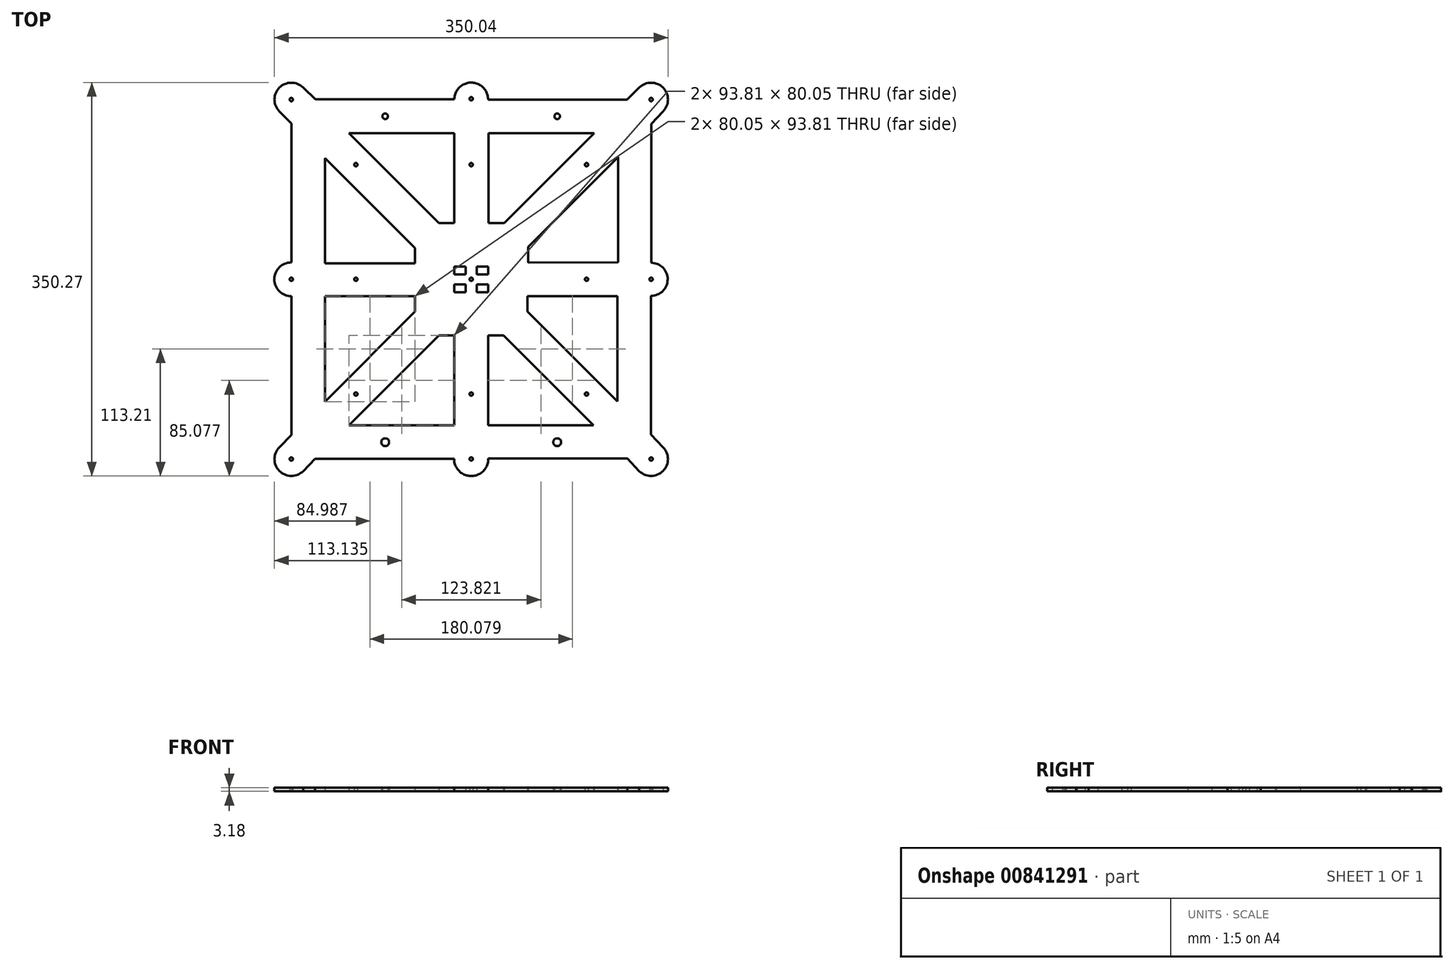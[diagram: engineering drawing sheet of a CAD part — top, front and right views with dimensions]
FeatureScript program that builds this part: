
annotation { "Feature Type Name" : "Feature", "Feature Type Description" : "" }
export const myFeature = defineFeature(function(context is Context, id is Id, definition is map)
    precondition{}
    {
        {
            var Q0;
            Q0=qCreatedBy(makeId("Top.planeOp"),FACE);
            var sketch = newSketch(context, id + "F0", { "sketchPlane" : qUnion([Q0])});
            skPoint(sketch, "E0.middle", {"position": v(0, 0) * mm});
            skLineSegment(sketch, "E1", {"start": v(-130.02, 107.83) * mm, "end": v(-130.02, 14.06) * mm});
            skLineSegment(sketch, "E2", {"start": v(-160.02, 138.65) * mm, "end": v(-160.02, 15.05) * mm});
            skLineSegment(sketch, "E3.MirrorCS", {"start": v(-138.62, 160.12) * mm, "end": v(-15.02, 160.12) * mm});
            skLineSegment(sketch, "E4.MirrorCS", {"start": v(-108.76, 130.12) * mm, "end": v(-14.99, 130.12) * mm});
            skLineSegment(sketch, "E5.MirrorCS", {"start": v(109.27, 130.02) * mm, "end": v(15.5, 130.02) * mm});
            skLineSegment(sketch, "E6.MirrorCS", {"start": v(160.27, 138.3) * mm, "end": v(160.27, 14.7) * mm});
            skLineSegment(sketch, "E7.MirrorCS", {"start": v(130.5, 108.82) * mm, "end": v(130.57, 15.05) * mm});
            skLineSegment(sketch, "E8.MirrorCS", {"start": v(-160, -138.65) * mm, "end": v(-160, -15.05) * mm});
            skLineSegment(sketch, "E9.MirrorCS", {"start": v(-130.04, -108.82) * mm, "end": v(-130.08, -15.05) * mm});
            skLineSegment(sketch, "E10.MirrorCS", {"start": v(-108.81, -130.03) * mm, "end": v(-15.04, -130.07) * mm});
            skLineSegment(sketch, "E11.MirrorCS", {"start": v(-138.84, -159.88) * mm, "end": v(-15.24, -159.88) * mm});
            skLineSegment(sketch, "E12.MirrorCS", {"start": v(108.82, -130.03) * mm, "end": v(15.05, -130.07) * mm});
            skLineSegment(sketch, "E13.MirrorCS", {"start": v(130.01, -108.8) * mm, "end": v(130.05, -15.03) * mm});
            skLineSegment(sketch, "E14.MirrorCS", {"start": v(160, -138.3) * mm, "end": v(160, -14.7) * mm});
            skLineSegment(sketch, "E15", {"start": v(-49.97, 14.06) * mm, "end": v(-130.02, 14.06) * mm});
            skLineSegment(sketch, "E16", {"start": v(-50.03, -15) * mm, "end": v(-130.08, -15.05) * mm});
            skLineSegment(sketch, "E17", {"start": v(-170.7, 149.5) * mm, "end": v(-160.02, 138.65) * mm});
            skLineSegment(sketch, "E18", {"start": v(-130.02, 107.83) * mm, "end": v(-49.97, 27.86) * mm});
            skLineSegment(sketch, "E19", {"start": v(-49.97, 27.86) * mm, "end": v(-49.97, 14.06) * mm});
            skLineSegment(sketch, "E20", {"start": v(-50.03, -15) * mm, "end": v(-50.03, -28.8) * mm});
            skLineSegment(sketch, "E21", {"start": v(-170.7, -149.5) * mm, "end": v(-160, -138.65) * mm});
            skLineSegment(sketch, "E22", {"start": v(-130.04, -108.82) * mm, "end": v(-50.03, -28.8) * mm});
            skLineSegment(sketch, "E23", {"start": v(-149.54, 170.75) * mm, "end": v(-138.62, 160.12) * mm});
            skLineSegment(sketch, "E24", {"start": v(-108.76, 130.12) * mm, "end": v(-28.79, 50.07) * mm});
            skLineSegment(sketch, "E25", {"start": v(-14.99, 130.12) * mm, "end": v(-14.99, 50.07) * mm});
            skLineSegment(sketch, "E26", {"start": v(-28.79, 50.07) * mm, "end": v(-14.99, 50.07) * mm});
            skLineSegment(sketch, "E27", {"start": v(15.5, 49.97) * mm, "end": v(29.3, 49.97) * mm});
            skLineSegment(sketch, "E28", {"start": v(15.5, 130.02) * mm, "end": v(15.5, 49.97) * mm});
            skLineSegment(sketch, "E29", {"start": v(-149.54, -170.75) * mm, "end": v(-138.84, -159.88) * mm});
            skLineSegment(sketch, "E30", {"start": v(-108.81, -130.03) * mm, "end": v(-28.8, -50.02) * mm});
            skLineSegment(sketch, "E31", {"start": v(-15, -50.02) * mm, "end": v(-15.04, -130.07) * mm});
            skLineSegment(sketch, "E32", {"start": v(15.01, -50.02) * mm, "end": v(15.05, -130.07) * mm});
            skLineSegment(sketch, "E33", {"start": v(-28.8, -50.02) * mm, "end": v(-15, -50.02) * mm});
            skLineSegment(sketch, "E34", {"start": v(15.01, -50.02) * mm, "end": v(28.8, -50.02) * mm});
            skLineSegment(sketch, "E35", {"start": v(149.54, 170.75) * mm, "end": v(138.62, 160.02) * mm});
            skLineSegment(sketch, "E36", {"start": v(109.27, 130.02) * mm, "end": v(29.3, 49.97) * mm});
            skLineSegment(sketch, "E37", {"start": v(50.52, 28.76) * mm, "end": v(130.5, 108.82) * mm});
            skLineSegment(sketch, "E38", {"start": v(160.27, 138.3) * mm, "end": v(170.7, 149.5) * mm});
            skLineSegment(sketch, "E39", {"start": v(130.57, 15.05) * mm, "end": v(50.52, 14.97) * mm});
            skLineSegment(sketch, "E40", {"start": v(50, -14.99) * mm, "end": v(130.05, -15.03) * mm});
            skLineSegment(sketch, "E41", {"start": v(170.7, -149.5) * mm, "end": v(160, -138.3) * mm});
            skLineSegment(sketch, "E42", {"start": v(130.01, -108.8) * mm, "end": v(50, -28.79) * mm});
            skLineSegment(sketch, "E43", {"start": v(108.82, -130.03) * mm, "end": v(28.8, -50.02) * mm});
            skLineSegment(sketch, "E44", {"start": v(149.54, -170.75) * mm, "end": v(138.84, -159.55) * mm});
            skLineSegment(sketch, "E45", {"start": v(50.52, 28.76) * mm, "end": v(50.52, 14.97) * mm});
            skLineSegment(sketch, "E46", {"start": v(50, -14.99) * mm, "end": v(50, -28.79) * mm});
            skArc(sketch, "E47", {"start": v(-149.54, 170.75) * mm, "mid": v(-170.63, 170.59) * mm, "end": v(-170.7, 149.5) * mm});
            skArc(sketch, "E48.MirrorCS", {"start": v(149.54, 170.75) * mm, "mid": v(170.63, 170.59) * mm, "end": v(170.7, 149.5) * mm});
            skArc(sketch, "E49.MirrorCS", {"start": v(-149.54, -170.75) * mm, "mid": v(-170.63, -170.59) * mm, "end": v(-170.7, -149.5) * mm});
            skArc(sketch, "E50.MirrorCS", {"start": v(149.54, -170.75) * mm, "mid": v(170.63, -170.59) * mm, "end": v(170.7, -149.5) * mm});
            skCircle(sketch, "E51", {"center": v(-160, 160) * mm, "radius": 1.5 * mm});
            skCircle(sketch, "E52.MirrorC", {"center": v(160, 160) * mm, "radius": 1.5 * mm});
            skArc(sketch, "E53", {"start": v(-160, -15.05) * mm, "mid": v(-175.04, -0.01) * mm, "end": v(-160.02, 15.05) * mm});
            skArc(sketch, "E54", {"start": v(160, -14.7) * mm, "mid": v(174.71, -0.13) * mm, "end": v(160.27, 14.7) * mm});
            skArc(sketch, "E55", {"start": v(-15.24, -159.88) * mm, "mid": v(0.16, -175.12) * mm, "end": v(15.24, -159.55) * mm});
            skLineSegment(sketch, "E56", {"start": v(15.24, -159.55) * mm, "end": v(138.84, -159.55) * mm});
            skArc(sketch, "E57", {"start": v(-15.02, 160.12) * mm, "mid": v(0.05, 175.15) * mm, "end": v(15.02, 160.02) * mm});
            skLineSegment(sketch, "E58", {"start": v(15.02, 160.02) * mm, "end": v(138.62, 160.02) * mm});
            skCircle(sketch, "E59", {"center": v(-160, 0) * mm, "radius": 1.5 * mm});
            skCircle(sketch, "E60.MirrorC", {"center": v(0, 160.72) * mm, "radius": 1.5 * mm});
            skCircle(sketch, "E61.MirrorC", {"center": v(160, 0) * mm, "radius": 1.5 * mm});
            skCircle(sketch, "E62.MirrorC", {"center": v(-160, -160) * mm, "radius": 1.5 * mm});
            skCircle(sketch, "E63", {"center": v(0, -159.88) * mm, "radius": 1.5 * mm});
            skCircle(sketch, "E64.MirrorC", {"center": v(160, -160) * mm, "radius": 1.5 * mm});
            skCircle(sketch, "E65", {"center": v(-76.5, 145.1) * mm, "radius": 2.5 * mm});
            skCircle(sketch, "E66.MirrorC", {"center": v(76.5, 145.1) * mm, "radius": 2.5 * mm});
            skCircle(sketch, "E67", {"center": v(-76.5, -145) * mm, "radius": 3.5 * mm});
            skCircle(sketch, "E68", {"center": v(76.5, -145) * mm, "radius": 3.5 * mm});
            skLineSegment(sketch, "E69.bottom", {"start": v(-5, -11.5) * mm, "end": v(-15, -11.5) * mm});
            skLineSegment(sketch, "E69.top", {"start": v(-5, -4.5) * mm, "end": v(-15, -4.5) * mm});
            skLineSegment(sketch, "E69.left", {"start": v(-5, -11.5) * mm, "end": v(-5, -4.5) * mm});
            skLineSegment(sketch, "E69.right", {"start": v(-15, -11.5) * mm, "end": v(-15, -4.5) * mm});
            skPoint(sketch, "E69.middle", {"position": v(-10, -8) * mm});
            skLineSegment(sketch, "E70.MirrorCS", {"start": v(5, -4.5) * mm, "end": v(15, -4.5) * mm});
            skLineSegment(sketch, "E71.MirrorCS", {"start": v(5, -11.5) * mm, "end": v(5, -4.5) * mm});
            skLineSegment(sketch, "E72.MirrorCS", {"start": v(5, -11.5) * mm, "end": v(15, -11.5) * mm});
            skLineSegment(sketch, "E73.MirrorCS", {"start": v(15, -11.5) * mm, "end": v(15, -4.5) * mm});
            skLineSegment(sketch, "E74.MirrorCS", {"start": v(-5, 4.5) * mm, "end": v(-15, 4.5) * mm});
            skLineSegment(sketch, "E75.MirrorCS", {"start": v(5, 4.5) * mm, "end": v(15, 4.5) * mm});
            skLineSegment(sketch, "E76.MirrorCS", {"start": v(-5, 11.5) * mm, "end": v(-5, 4.5) * mm});
            skLineSegment(sketch, "E77.MirrorCS", {"start": v(5, 11.5) * mm, "end": v(5, 4.5) * mm});
            skLineSegment(sketch, "E78.MirrorCS", {"start": v(5, 11.5) * mm, "end": v(15, 11.5) * mm});
            skLineSegment(sketch, "E79.MirrorCS", {"start": v(15, 11.5) * mm, "end": v(15, 4.5) * mm});
            skLineSegment(sketch, "E80.MirrorCS", {"start": v(-15, 11.5) * mm, "end": v(-15, 4.5) * mm});
            skLineSegment(sketch, "E81.MirrorCS", {"start": v(-5, 11.5) * mm, "end": v(-15, 11.5) * mm});
            skCircle(sketch, "E82", {"center": v(0, 0) * mm, "radius": 1.5 * mm});
            skCircle(sketch, "E83", {"center": v(102.59, 102.1) * mm, "radius": 1.5 * mm});
            skCircle(sketch, "E84", {"center": v(0, 102.1) * mm, "radius": 1.5 * mm});
            skCircle(sketch, "E85.MirrorC", {"center": v(-102.59, 102.1) * mm, "radius": 1.5 * mm});
            skCircle(sketch, "E86", {"center": v(102.59, 0) * mm, "radius": 1.5 * mm});
            skCircle(sketch, "E87.MirrorC", {"center": v(102.59, -102.1) * mm, "radius": 1.5 * mm});
            skCircle(sketch, "E88.MirrorC", {"center": v(0, -102.1) * mm, "radius": 1.5 * mm});
            skCircle(sketch, "E89.MirrorC", {"center": v(-102.59, -102.1) * mm, "radius": 1.5 * mm});
            skCircle(sketch, "E90.MirrorC", {"center": v(-102.59, 0) * mm, "radius": 1.5 * mm});
            skSolve(sketch);
        }
        {
            var Q0;
            Q0=makeQuery(id+"F0.imprint","IMPRINT",FACE,{"disambiguationData":[TD([[makeQuery(id+"F0.imprint","IMPRINT",EDGE,{"derivedFrom":sQuery(id+"F0.wireOp",EDGE,"E1")}),-1.0]])]});
            extrude(context, id + "F1", {"entities" : qUnion([Q0]), "depth" : 3.17 * mm, "offsetDistance" : 25 * mm});
        }
    });
